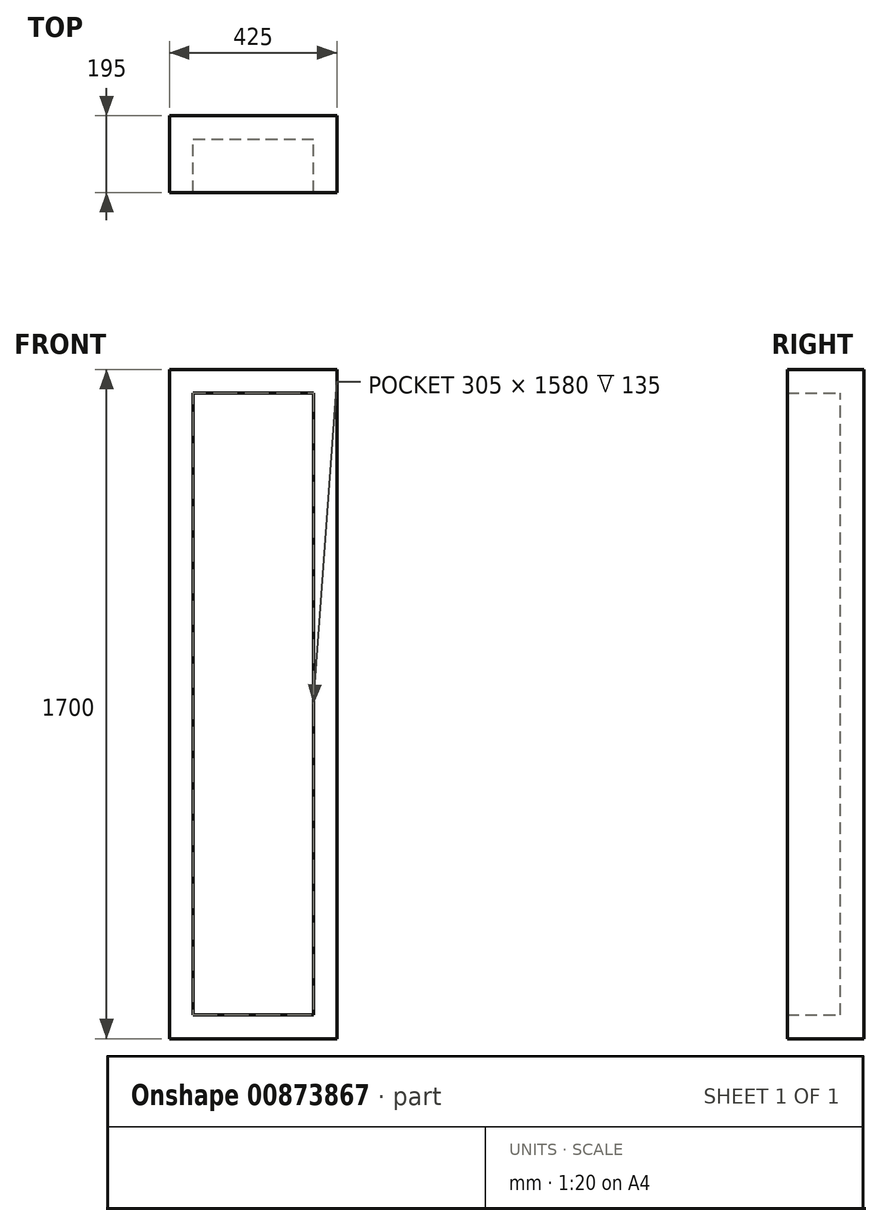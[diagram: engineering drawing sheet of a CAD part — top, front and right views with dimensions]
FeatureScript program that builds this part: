
annotation { "Feature Type Name" : "Feature", "Feature Type Description" : "" }
export const myFeature = defineFeature(function(context is Context, id is Id, definition is map)
    precondition{}
    {
        {
            var Q0;
            Q0=qCreatedBy(makeId("Front.planeOp"),FACE);
            var sketch = newSketch(context, id + "F0", { "sketchPlane" : qUnion([Q0])});
            skLineSegment(sketch, "E0.bottom", {"start": v(0, 0) * mm, "end": v(45.54, 0) * mm});
            skLineSegment(sketch, "E0.top", {"start": v(0, 44.11) * mm, "end": v(45.54, 44.11) * mm});
            skLineSegment(sketch, "E0.left", {"start": v(0, 0) * mm, "end": v(0, 44.11) * mm});
            skLineSegment(sketch, "E0.right", {"start": v(45.54, 0) * mm, "end": v(45.54, 44.11) * mm});
            skSolve(sketch);
        }
        {
            var Q0;
            Q0=makeQuery(id+"F0.imprint","IMPRINT",FACE,{"disambiguationData":[TD([[makeQuery(id+"F0.imprint","IMPRINT",EDGE,{"derivedFrom":sQuery(id+"F0.wireOp",EDGE,"E0.bottom")}),1.0]])]});
            extrude(context, id + "F1", {"entities" : qUnion([Q0]), "depth" : 195 * mm, "offsetDistance" : 25 * mm});
        }
        {
            var Q0;
            Q0=makeQuery(id+"F1.opExtrude","SWEPT_FACE",FACE,{"disambiguationData":[OSD([sQuery(id+"F0.wireOp",EDGE,"E0.bottom")])]});
            extrude(context, id + "F2", {"entities" : qUnion([Q0]), "operationType" : NewBodyOperationType.ADD, "oppositeDirection" : true, "depth" : 1700 * mm, "offsetDistance" : 25 * mm});
        }
        {
            var Q0;
            {var subQ0=sQuery(id+"F0.wireOp",EDGE,"E0.left");Q0=makeQuery(id+"F2.boolean.opBoolean","MERGE",FACE,{"derivedFrom":[makeQuery(id+"F1.opExtrude","SWEPT_FACE",FACE,{"disambiguationData":[OSD([subQ0])]}),makeQuery(id+"F2.opExtrude","SWEPT_FACE",FACE,{"disambiguationData":[OSD([sQuery(id+"F0.wireOp",EDGE,"E0.bottom"),subQ0])]})]});}
            extrude(context, id + "F3", {"entities" : qUnion([Q0]), "operationType" : NewBodyOperationType.ADD, "oppositeDirection" : true, "depth" : 425 * mm, "offsetDistance" : 25 * mm});
        }
        {
            var Q0;
            {var subQ0=sQuery(id+"F0.wireOp",EDGE,"E0.left");var subQ1=sQuery(id+"F0.wireOp",EDGE,"E0.bottom");Q0=makeQuery(id+"F3.boolean.opBoolean","MERGE",FACE,{"derivedFrom":[makeQuery(id+"F2.boolean.opBoolean","MERGE",FACE,{"derivedFrom":[makeQuery(id+"F1.opExtrude","CAP_FACE",FACE,{"disambiguationData":[OSD([subQ1,sQuery(id+"F0.wireOp",EDGE,"E0.top"),subQ0,sQuery(id+"F0.wireOp",EDGE,"E0.right")])],"isStart":false}),makeQuery(id+"F2.opExtrude","SWEPT_FACE",FACE,{"disambiguationData":[OSD([subQ1]),TDD([makeQuery(id+"F1.opExtrude","CAP_EDGE",EDGE,{"disambiguationData":[OSD([subQ1])],"isStart":false})])]})]}),makeQuery(id+"F3.opExtrude","SWEPT_FACE",FACE,{"disambiguationData":[OSD([subQ1,subQ0]),TDD([makeQuery(id+"F2.boolean.opBoolean","MERGE",EDGE,{"derivedFrom":[makeQuery(id+"F1.opExtrude","CAP_EDGE",EDGE,{"disambiguationData":[OSD([subQ0])],"isStart":false}),makeQuery(id+"F2.opExtrude","SWEPT_EDGE",EDGE,{"disambiguationData":[OSD([subQ1,subQ0]),TDD([makeQuery(id+"F1.opExtrude","CAP_VERTEX",VERTEX,{"disambiguationData":[OSD([subQ1,subQ0])],"isStart":false})])]})]})])]})]});}
            shell(context, id + "F4", {"entities" : qUnion([Q0]), "thickness" : 60 * mm});
        }
    });
